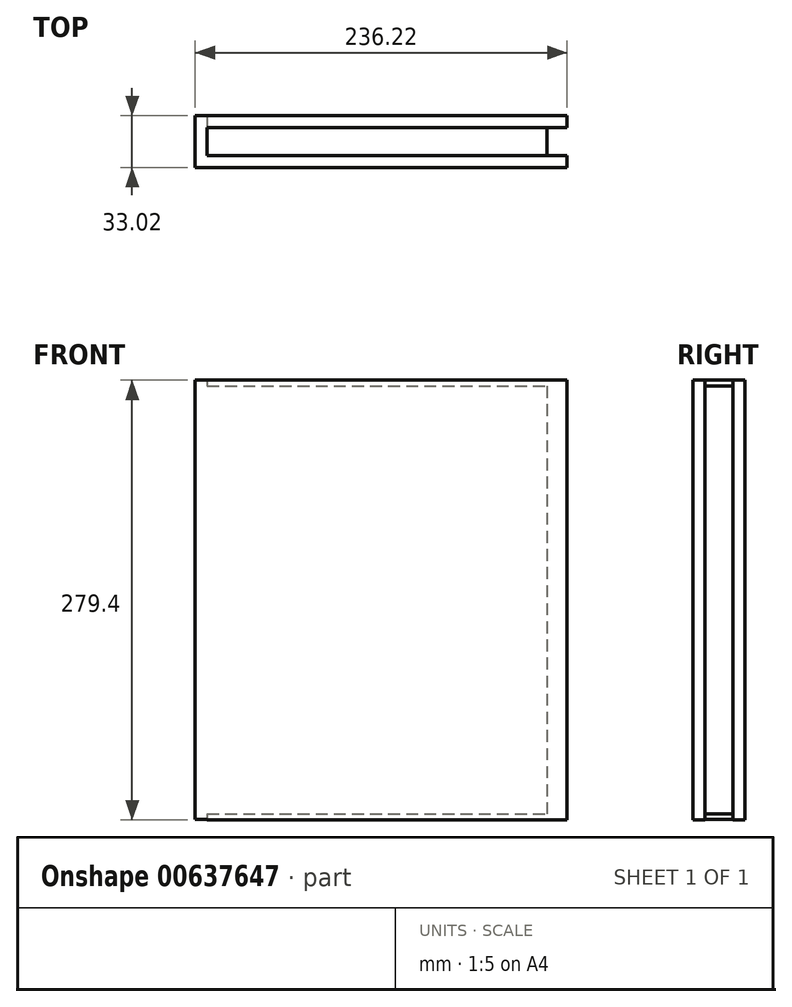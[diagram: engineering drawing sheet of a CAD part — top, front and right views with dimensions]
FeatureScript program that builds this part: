
annotation { "Feature Type Name" : "Feature", "Feature Type Description" : "" }
export const myFeature = defineFeature(function(context is Context, id is Id, definition is map)
    precondition{}
    {
        {
            var Q0;
            Q0=qCreatedBy(makeId("Front.planeOp"),FACE);
            var sketch = newSketch(context, id + "F0", { "sketchPlane" : qUnion([Q0])});
            skLineSegment(sketch, "E0.bottom", {"start": v(-80.75, 115.39) * mm, "end": v(135.15, 115.39) * mm});
            skLineSegment(sketch, "E0.top", {"start": v(-80.75, -156.4) * mm, "end": v(135.15, -156.4) * mm});
            skLineSegment(sketch, "E0.left", {"start": v(-80.75, 115.39) * mm, "end": v(-80.75, -156.4) * mm});
            skLineSegment(sketch, "E0.right", {"start": v(135.15, 115.39) * mm, "end": v(135.15, -156.4) * mm});
            skSolve(sketch);
        }
        {
            var Q0;
            Q0 = qSketchRegion(id + "F0", true);
            extrude(context, id + "F1", {"entities" : qUnion([Q0]), "depth" : 17.78 * mm, "offsetDistance" : 25.4 * mm});
        }
        {
            var Q0;
            Q0=makeQuery(id+"F1.opExtrude","CAP_FACE",FACE,{"disambiguationData":[OSD([sQuery(id+"F0.wireOp",EDGE,"E0.bottom"),sQuery(id+"F0.wireOp",EDGE,"E0.top"),sQuery(id+"F0.wireOp",EDGE,"E0.left"),sQuery(id+"F0.wireOp",EDGE,"E0.right")])],"isStart":false});
            var sketch = newSketch(context, id + "F2", { "sketchPlane" : qUnion([Q0])});
            skLineSegment(sketch, "E1.right", {"start": v(147.85, 119.2) * mm, "end": v(147.85, -160.2) * mm});
            skLineSegment(sketch, "E2", {"start": v(147.85, 119.2) * mm, "end": v(-80.75, 119.2) * mm});
            skLineSegment(sketch, "E3", {"start": v(-80.75, 119.2) * mm, "end": v(-80.75, -159.85) * mm});
            skLineSegment(sketch, "E4", {"start": v(147.85, -160.2) * mm, "end": v(-80.75, -159.85) * mm});
            skSolve(sketch);
        }
        {
            var Q0;
            Q0=makeQuery(id+"F1.opExtrude","CAP_FACE",FACE,{"disambiguationData":[OSD([sQuery(id+"F0.wireOp",EDGE,"E0.bottom"),sQuery(id+"F0.wireOp",EDGE,"E0.top"),sQuery(id+"F0.wireOp",EDGE,"E0.left"),sQuery(id+"F0.wireOp",EDGE,"E0.right")])],"isStart":true});
            var sketch = newSketch(context, id + "F3", { "sketchPlane" : qUnion([Q0])});
            skLineSegment(sketch, "E5.bottom", {"start": v(-147.85, 119.2) * mm, "end": v(80.75, 119.2) * mm});
            skLineSegment(sketch, "E5.top", {"start": v(-147.85, -160.2) * mm, "end": v(80.75, -160.2) * mm});
            skLineSegment(sketch, "E5.left", {"start": v(-147.85, 119.2) * mm, "end": v(-147.85, -160.2) * mm});
            skLineSegment(sketch, "E5.right", {"start": v(80.75, 119.2) * mm, "end": v(80.75, -160.2) * mm});
            skSolve(sketch);
        }
        {
            var Q0;
            Q0 = qSketchRegion(id + "F2", true);
            extrude(context, id + "F4", {"entities" : qUnion([Q0]), "operationType" : NewBodyOperationType.ADD, "depth" : 7.62 * mm, "offsetDistance" : 25.4 * mm});
        }
        {
            var Q0;
            Q0 = qSketchRegion(id + "F3", true);
            extrude(context, id + "F5", {"entities" : qUnion([Q0]), "operationType" : NewBodyOperationType.ADD, "depth" : 7.62 * mm, "offsetDistance" : 25.4 * mm});
        }
        {
            var Q0;
            Q0=makeQuery(id+"F5.boolean.opBoolean","MERGE",FACE,{"derivedFrom":[makeQuery(id+"F4.boolean.opBoolean","MERGE",FACE,{"derivedFrom":[makeQuery(id+"F1.opExtrude","SWEPT_FACE",FACE,{"disambiguationData":[OSD([sQuery(id+"F0.wireOp",EDGE,"E0.left")])]}),makeQuery(id+"F4.opExtrude","SWEPT_FACE",FACE,{"disambiguationData":[OSD([sQuery(id+"F2.wireOp",EDGE,"E3")])]})]}),makeQuery(id+"F5.opExtrude","SWEPT_FACE",FACE,{"disambiguationData":[OSD([sQuery(id+"F3.wireOp",EDGE,"E5.right")])]})]});
            var sketch = newSketch(context, id + "F6", { "sketchPlane" : qUnion([Q0])});
            skLineSegment(sketch, "E6.bottom", {"start": v(-7.62, 119.2) * mm, "end": v(25.4, 119.2) * mm});
            skLineSegment(sketch, "E6.top", {"start": v(-7.62, -159.85) * mm, "end": v(25.4, -159.85) * mm});
            skLineSegment(sketch, "E6.left", {"start": v(-7.62, 119.2) * mm, "end": v(-7.62, -159.85) * mm});
            skLineSegment(sketch, "E6.right", {"start": v(25.4, 119.2) * mm, "end": v(25.4, -159.85) * mm});
            skSolve(sketch);
        }
        {
            var Q0;
            Q0 = qSketchRegion(id + "F6", true);
            extrude(context, id + "F7", {"entities" : qUnion([Q0]), "operationType" : NewBodyOperationType.ADD, "depth" : 7.62 * mm, "offsetDistance" : 25.4 * mm});
        }
    });
